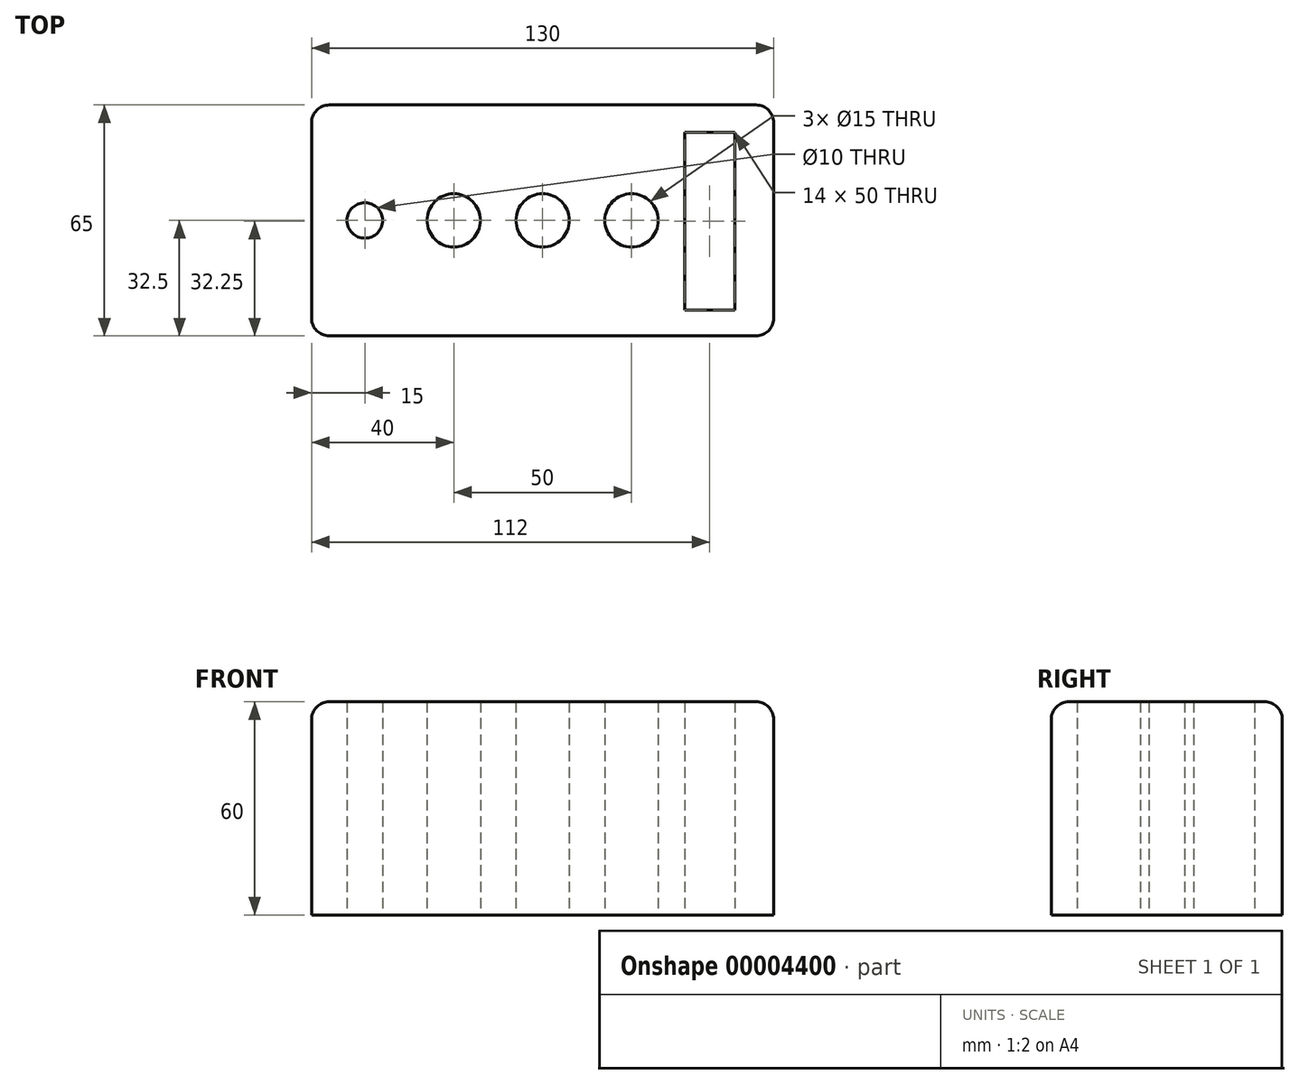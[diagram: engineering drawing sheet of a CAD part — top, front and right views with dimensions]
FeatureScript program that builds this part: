
annotation { "Feature Type Name" : "Feature", "Feature Type Description" : "" }
export const myFeature = defineFeature(function(context is Context, id is Id, definition is map)
    precondition{}
    {
        {
            var Q0;
            Q0=qCreatedBy(makeId("Top.planeOp"),FACE);
            var sketch = newSketch(context, id + "F0", { "sketchPlane" : qUnion([Q0])});
            skLineSegment(sketch, "E0.bottom", {"start": v(5, 0) * mm, "end": v(125, 0) * mm});
            skLineSegment(sketch, "E0.top", {"start": v(5, 65) * mm, "end": v(125, 65) * mm});
            skLineSegment(sketch, "E0.left", {"start": v(0, 5) * mm, "end": v(0, 60) * mm});
            skLineSegment(sketch, "E0.right", {"start": v(130, 5) * mm, "end": v(130, 60) * mm});
            skCircle(sketch, "E1", {"center": v(15, 32.5) * mm, "radius": 5 * mm});
            skCircle(sketch, "E2", {"center": v(40, 32.5) * mm, "radius": 7.5 * mm});
            skCircle(sketch, "E3", {"center": v(65, 32.5) * mm, "radius": 7.5 * mm});
            skCircle(sketch, "E4", {"center": v(90, 32.5) * mm, "radius": 7.5 * mm});
            skLineSegment(sketch, "E5.bottom", {"start": v(105, 57.25) * mm, "end": v(119, 57.25) * mm});
            skLineSegment(sketch, "E5.top", {"start": v(105, 7.25) * mm, "end": v(119, 7.25) * mm});
            skLineSegment(sketch, "E5.left", {"start": v(105, 57.25) * mm, "end": v(105, 7.25) * mm});
            skLineSegment(sketch, "E5.right", {"start": v(119, 57.25) * mm, "end": v(119, 7.25) * mm});
            skPoint(sketch, "E6.visualSharp", {"position": v(0, 65) * mm});
            skArc(sketch, "E6.filletArc", {"start": v(5, 65) * mm, "mid": v(1.46, 63.54) * mm, "end": v(0, 60) * mm});
            skPoint(sketch, "E7.visualSharp", {"position": v(0, 0) * mm});
            skArc(sketch, "E7.filletArc", {"start": v(0, 5) * mm, "mid": v(1.46, 1.46) * mm, "end": v(5, 0) * mm});
            skPoint(sketch, "E8.visualSharp", {"position": v(130, 0) * mm});
            skArc(sketch, "E8.filletArc", {"start": v(125, 0) * mm, "mid": v(128.54, 1.46) * mm, "end": v(130, 5) * mm});
            skPoint(sketch, "E9.visualSharp", {"position": v(130, 65) * mm});
            skArc(sketch, "E9.filletArc", {"start": v(130, 60) * mm, "mid": v(128.54, 63.54) * mm, "end": v(125, 65) * mm});
            skSolve(sketch);
        }
        {
            var Q0;
            Q0=makeQuery(id+"F0.imprint","IMPRINT",FACE,{"disambiguationData":[TD([[makeQuery(id+"F0.imprint","IMPRINT",EDGE,{"derivedFrom":sQuery(id+"F0.wireOp",EDGE,"E0.bottom")}),1.0]])]});
            extrude(context, id + "F1", {"entities" : qUnion([Q0]), "depth" : 60 * mm});
        }
        {
            var Q0;
            Q0=makeQuery(id+"F1.opExtrude","CAP_EDGE",EDGE,{"disambiguationData":[OSD([sQuery(id+"F0.wireOp",EDGE,"E0.bottom")])],"isStart":false});
            var Q1;
            Q1=makeQuery(id+"F1.opExtrude","CAP_EDGE",EDGE,{"disambiguationData":[OSD([sQuery(id+"F0.wireOp",EDGE,"E7.filletArc")])],"isStart":false});
            fillet(context, id + "F2", {"entities" : qUnion([Q0, Q1]), "radius" : 5 * mm, "tangentPropagation" : true, "allowEdgeOverflow" : false});
        }
    });
